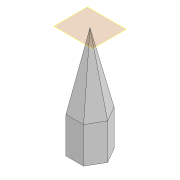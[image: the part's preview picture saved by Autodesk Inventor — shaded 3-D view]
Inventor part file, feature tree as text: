
AUTODESK INVENTOR PART (.ipt)
format: ipt  version: 2022 (Build 260153000, 153)  size: 207,872 bytes
history: native  units: mm
features: sketch x2, extrude x1, plane x1, loft x1, other x1
ambient origin geometry x8: Origin, YZ Plane, XZ Plane, XY Plane, X Axis, Y Axis, Z Axis, Center Point
bodies: Solid1 (feature_tree)
feature tree (6):
  extrude  "Extrusion1"  Depth=17.0mm TaperAngle=0.0deg
  plane  "Work Plane1"
  loft  "Loft1"
  sketch  "Sketch1"  dims[d0=17.0mm d1=20.0mm d2=0.0mm]
  sketch  "Sketch2"  dims[d3=40.0mm d4=0.0mm d5=90.0deg d6=0.0mm d7=90.0deg]
  other  "Edges1"
